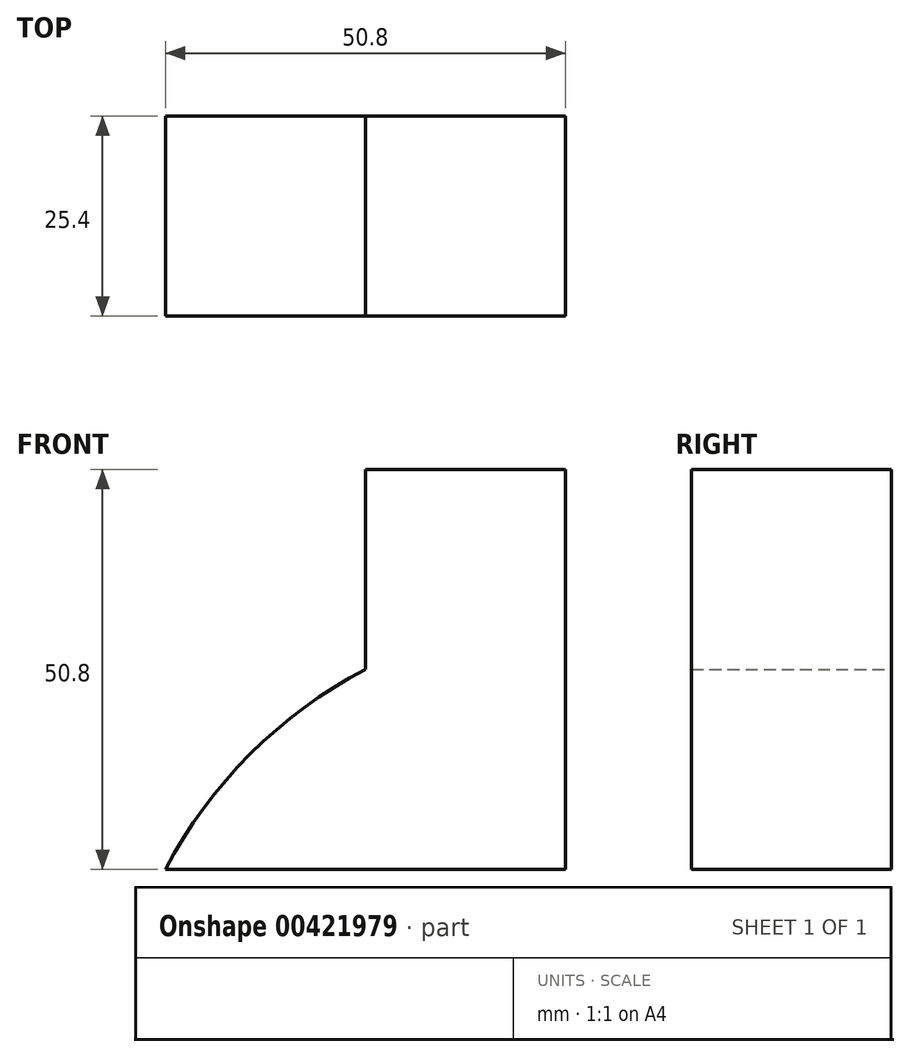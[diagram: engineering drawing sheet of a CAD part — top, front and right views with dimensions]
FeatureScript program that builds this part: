
annotation { "Feature Type Name" : "Feature", "Feature Type Description" : "" }
export const myFeature = defineFeature(function(context is Context, id is Id, definition is map)
    precondition{}
    {
        {
            var Q0;
            Q0=qCreatedBy(makeId("Front.planeOp"),FACE);
            var sketch = newSketch(context, id + "F0", { "sketchPlane" : qUnion([Q0])});
            skLineSegment(sketch, "E0", {"start": v(0, 0) * mm, "end": v(-50.8, 0) * mm});
            skLineSegment(sketch, "E1", {"start": v(0, 0) * mm, "end": v(0, 50.8) * mm});
            skLineSegment(sketch, "E2", {"start": v(0, 50.8) * mm, "end": v(-25.4, 50.8) * mm});
            skLineSegment(sketch, "E3", {"start": v(-25.4, 50.8) * mm, "end": v(-25.4, 25.4) * mm});
            skArc(sketch, "E4", {"start": v(-25.4, 25.4) * mm, "mid": v(-40.06, 14.66) * mm, "end": v(-50.8, 0) * mm});
            skSolve(sketch);
        }
        {
            var Q0;
            Q0=makeQuery(id+"F0.imprint","IMPRINT",FACE,{"disambiguationData":[TD([[makeQuery(id+"F0.imprint","IMPRINT",EDGE,{"derivedFrom":sQuery(id+"F0.wireOp",EDGE,"E0")}),-1.0]])]});
            extrude(context, id + "F1", {"entities" : qUnion([Q0]), "depth" : 25.4 * mm});
        }
    });
